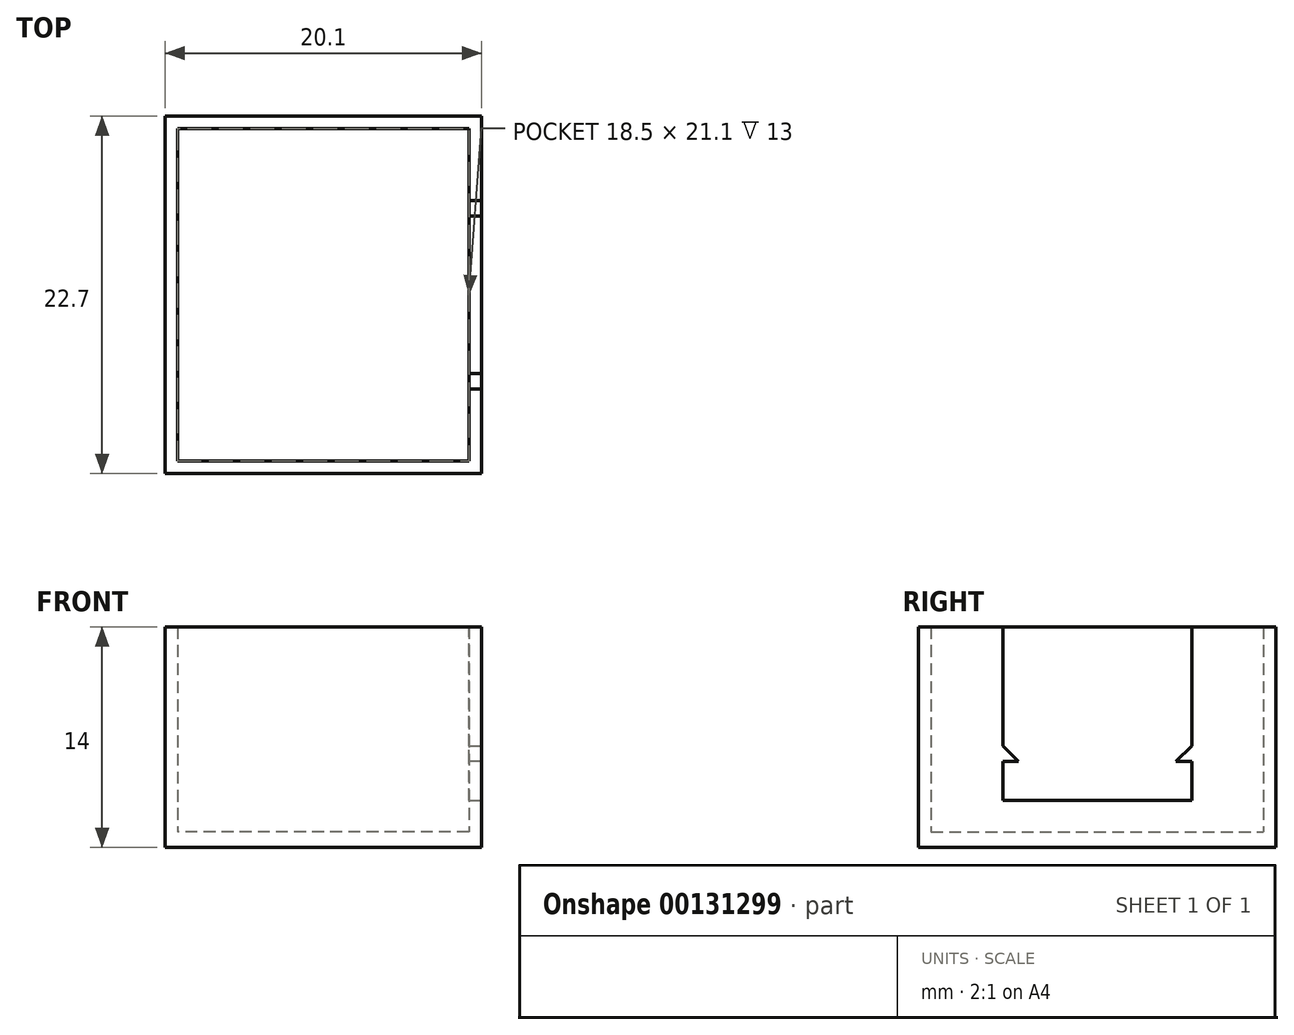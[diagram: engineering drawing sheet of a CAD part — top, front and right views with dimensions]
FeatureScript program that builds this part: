
annotation { "Feature Type Name" : "Feature", "Feature Type Description" : "" }
export const myFeature = defineFeature(function(context is Context, id is Id, definition is map)
    precondition{}
    {
        {
            var Q0;
            Q0=qCreatedBy(makeId("Top.planeOp"),FACE);
            var sketch = newSketch(context, id + "F0", { "sketchPlane" : qUnion([Q0])});
            skLineSegment(sketch, "E0.bottom", {"start": v(9.25, -10.55) * mm, "end": v(-9.25, -10.55) * mm});
            skLineSegment(sketch, "E0.top", {"start": v(9.25, 10.55) * mm, "end": v(-9.25, 10.55) * mm});
            skLineSegment(sketch, "E0.left", {"start": v(9.25, -10.55) * mm, "end": v(9.25, 10.55) * mm});
            skLineSegment(sketch, "E0.right", {"start": v(-9.25, -10.55) * mm, "end": v(-9.25, 10.55) * mm});
            skPoint(sketch, "E0.middle", {"position": v(0, 0) * mm});
            skLineSegment(sketch, "E1.0", {"start": v(-10.05, -11.35) * mm, "end": v(-10.05, 11.35) * mm});
            skLineSegment(sketch, "E1.1", {"start": v(10.05, -11.35) * mm, "end": v(-10.05, -11.35) * mm});
            skLineSegment(sketch, "E1.2", {"start": v(10.05, -11.35) * mm, "end": v(10.05, 11.35) * mm});
            skLineSegment(sketch, "E1.3", {"start": v(10.05, 11.35) * mm, "end": v(-10.05, 11.35) * mm});
            skSolve(sketch);
        }
        {
            var Q0;
            Q0 = qSketchRegion(id + "F0", true);
            extrude(context, id + "F1", {"entities" : qUnion([Q0]), "depth" : 14 * mm});
        }
        {
            var Q0;
            Q0=makeQuery(id+"F0.imprint","IMPRINT",FACE,{"disambiguationData":[TD([[makeQuery(id+"F0.imprint","IMPRINT",EDGE,{"derivedFrom":sQuery(id+"F0.wireOp",EDGE,"E0.bottom")}),-1.0]])]});
            extrude(context, id + "F2", {"entities" : qUnion([Q0]), "operationType" : NewBodyOperationType.ADD, "depth" : 1 * mm});
        }
        {
            var Q0;
            Q0=makeQuery(id+"F1.opExtrude","CAP_FACE",FACE,{"disambiguationData":[OSD([sQuery(id+"F0.wireOp",EDGE,"E0.bottom"),sQuery(id+"F0.wireOp",EDGE,"E0.top"),sQuery(id+"F0.wireOp",EDGE,"E0.left"),sQuery(id+"F0.wireOp",EDGE,"E0.right"),sQuery(id+"F0.wireOp",EDGE,"E1.0"),sQuery(id+"F0.wireOp",EDGE,"E1.1"),sQuery(id+"F0.wireOp",EDGE,"E1.2"),sQuery(id+"F0.wireOp",EDGE,"E1.3")])],"isStart":false});
            var sketch = newSketch(context, id + "F3", { "sketchPlane" : qUnion([Q0])});
            skLineSegment(sketch, "E2.bottom", {"start": v(9.25, -6) * mm, "end": v(10.85, -6) * mm});
            skLineSegment(sketch, "E2.top", {"start": v(9.25, 6) * mm, "end": v(10.85, 6) * mm});
            skLineSegment(sketch, "E2.left", {"start": v(9.25, -6) * mm, "end": v(9.25, 6) * mm});
            skLineSegment(sketch, "E2.right", {"start": v(10.85, -6) * mm, "end": v(10.85, 6) * mm});
            skPoint(sketch, "E2.middle", {"position": v(10.05, 0) * mm});
            skSolve(sketch);
        }
        {
            var Q0;
            {var subQ0=sQuery(id+"F3.wireOp",EDGE,"E2.left");Q0=makeQuery(id+"F3.imprint","IMPRINT",FACE,{"disambiguationData":[TD([[makeQuery(id+"F3.imprint","IMPRINT",EDGE,{"derivedFrom":subQ0}),-1.0]])]});}
            extrude(context, id + "F4", {"entities" : qUnion([Q0]), "operationType" : NewBodyOperationType.REMOVE, "oppositeDirection" : true, "depth" : 11 * mm});
        }
        {
            var Q0;
            Q0=makeQuery(id+"F4.boolean.opBoolean","COPY",FACE,{"derivedFrom":makeQuery(id+"F4.opExtrude","SWEPT_FACE",FACE,{"disambiguationData":[OSD([sQuery(id+"F3.wireOp",EDGE,"E2.top")])]})});
            var sketch = newSketch(context, id + "F5", { "sketchPlane" : qUnion([Q0])});
            skLineSegment(sketch, "E3.bottom", {"start": v(10.05, 5.45) * mm, "end": v(9.25, 5.45) * mm});
            skLineSegment(sketch, "E3.top", {"start": v(10.05, 7.45) * mm, "end": v(9.25, 7.45) * mm});
            skLineSegment(sketch, "E3.left", {"start": v(10.05, 5.45) * mm, "end": v(10.05, 7.45) * mm});
            skLineSegment(sketch, "E3.right", {"start": v(9.25, 5.45) * mm, "end": v(9.25, 7.45) * mm});
            skSolve(sketch);
        }
        {
            var Q0;
            Q0=makeQuery(id+"F5.imprint","IMPRINT",FACE,{"disambiguationData":[TD([[makeQuery(id+"F5.imprint","IMPRINT",EDGE,{"derivedFrom":sQuery(id+"F5.wireOp",EDGE,"E3.bottom")}),-1.0]])]});
            extrude(context, id + "F6", {"entities" : qUnion([Q0]), "operationType" : NewBodyOperationType.ADD, "depth" : 1 * mm});
        }
        {
            var Q0;
            Q0=makeQuery(id+"F4.boolean.opBoolean","COPY",FACE,{"derivedFrom":makeQuery(id+"F4.opExtrude","SWEPT_FACE",FACE,{"disambiguationData":[OSD([sQuery(id+"F3.wireOp",EDGE,"E2.bottom")])]})});
            var sketch = newSketch(context, id + "F7", { "sketchPlane" : qUnion([Q0])});
            skLineSegment(sketch, "E4.bottom", {"start": v(-10.05, 5.45) * mm, "end": v(-9.25, 5.45) * mm});
            skLineSegment(sketch, "E4.top", {"start": v(-10.05, 7.45) * mm, "end": v(-9.25, 7.45) * mm});
            skLineSegment(sketch, "E4.left", {"start": v(-10.05, 5.45) * mm, "end": v(-10.05, 7.45) * mm});
            skLineSegment(sketch, "E4.right", {"start": v(-9.25, 5.45) * mm, "end": v(-9.25, 7.45) * mm});
            skSolve(sketch);
        }
        {
            var Q0;
            Q0=makeQuery(id+"F7.imprint","IMPRINT",FACE,{"disambiguationData":[TD([[makeQuery(id+"F7.imprint","IMPRINT",EDGE,{"derivedFrom":sQuery(id+"F7.wireOp",EDGE,"E4.bottom")}),1.0]])]});
            extrude(context, id + "F8", {"entities" : qUnion([Q0]), "operationType" : NewBodyOperationType.ADD, "depth" : 1 * mm});
        }
        {
            var Q0;
            Q0=makeQuery(id+"F6.opExtrude","CAP_EDGE",EDGE,{"disambiguationData":[OSD([sQuery(id+"F5.wireOp",EDGE,"E3.top")])],"isStart":false});
            var Q1;
            Q1=makeQuery(id+"F8.opExtrude","CAP_EDGE",EDGE,{"disambiguationData":[OSD([sQuery(id+"F7.wireOp",EDGE,"E4.top")])],"isStart":false});
            chamfer(context, id + "F9", {"entities" : qUnion([Q0, Q1]), "width" : 2 * mm, "tangentPropagation" : true});
        }
    });
